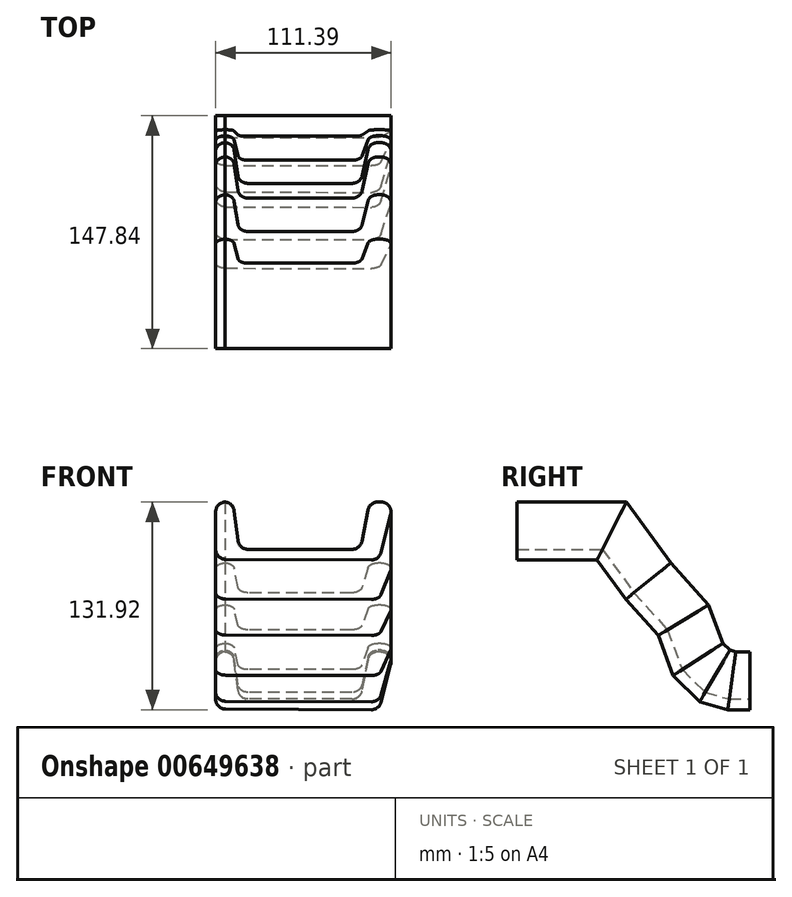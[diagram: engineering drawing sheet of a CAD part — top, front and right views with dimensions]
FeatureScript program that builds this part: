
annotation { "Feature Type Name" : "Feature", "Feature Type Description" : "" }
export const myFeature = defineFeature(function(context is Context, id is Id, definition is map)
    precondition{}
    {
        {
            var Q0;
            Q0=qCreatedBy(makeId("Front.planeOp"),FACE);
            var sketch = newSketch(context, id + "F0", { "sketchPlane" : qUnion([Q0])});
            skLineSegment(sketch, "E0", {"start": v(-51.67, 0) * mm, "end": v(-51.67, 23.72) * mm});
            skLineSegment(sketch, "E1", {"start": v(-46.16, 30.07) * mm, "end": v(-45.32, 30.07) * mm});
            skLineSegment(sketch, "E2", {"start": v(-39.86, 24.51) * mm, "end": v(-37.47, 5.56) * mm});
            skLineSegment(sketch, "E3", {"start": v(-31.17, 0) * mm, "end": v(34.97, 0) * mm});
            skLineSegment(sketch, "E4", {"start": v(41.2, 5.14) * mm, "end": v(45.05, 24.92) * mm});
            skLineSegment(sketch, "E5", {"start": v(51.29, 30.05) * mm, "end": v(53.37, 30.05) * mm});
            skLineSegment(sketch, "E6", {"start": v(59.53, 22.13) * mm, "end": v(53.36, -1.95) * mm});
            skLineSegment(sketch, "E7", {"start": v(47.18, -6.73) * mm, "end": v(-45.35, -6.35) * mm});
            skPoint(sketch, "E8.visualSharp", {"position": v(-51.67, 30.07) * mm});
            skArc(sketch, "E8.filletArc", {"start": v(-45.32, 30.07) * mm, "mid": v(-49.81, 28.2) * mm, "end": v(-51.67, 23.72) * mm});
            skPoint(sketch, "E9.visualSharp", {"position": v(61.56, 30.05) * mm});
            skArc(sketch, "E9.filletArc", {"start": v(59.53, 22.13) * mm, "mid": v(58.4, 27.6) * mm, "end": v(53.37, 30.05) * mm});
            skPoint(sketch, "E10.visualSharp", {"position": v(46.05, 30.05) * mm});
            skArc(sketch, "E10.filletArc", {"start": v(51.29, 30.05) * mm, "mid": v(47.25, 28.6) * mm, "end": v(45.05, 24.92) * mm});
            skPoint(sketch, "E11.visualSharp", {"position": v(52.13, -6.75) * mm});
            skArc(sketch, "E11.filletArc", {"start": v(47.18, -6.73) * mm, "mid": v(51.09, -5.4) * mm, "end": v(53.36, -1.95) * mm});
            skPoint(sketch, "E12.visualSharp", {"position": v(-40.57, 30.07) * mm});
            skArc(sketch, "E12.filletArc", {"start": v(-39.86, 24.51) * mm, "mid": v(-41.96, 28.48) * mm, "end": v(-46.16, 30.07) * mm});
            skPoint(sketch, "E13.visualSharp", {"position": v(-51.67, -6.32) * mm});
            skArc(sketch, "E13.filletArc", {"start": v(-51.67, 0) * mm, "mid": v(-49.82, -4.48) * mm, "end": v(-45.35, -6.35) * mm});
            skPoint(sketch, "E14.visualSharp", {"position": v(-36.77, 0) * mm});
            skArc(sketch, "E14.filletArc", {"start": v(-37.47, 5.56) * mm, "mid": v(-35.37, 1.59) * mm, "end": v(-31.17, 0) * mm});
            skPoint(sketch, "E15.visualSharp", {"position": v(40.2, 0) * mm});
            skArc(sketch, "E15.filletArc", {"start": v(34.97, 0) * mm, "mid": v(39, 1.45) * mm, "end": v(41.2, 5.14) * mm});
            skSolve(sketch);
        }
        {
            var Q0;
            Q0=qCreatedBy(makeId("Right.planeOp"),FACE);
            var sketch = newSketch(context, id + "F1", { "sketchPlane" : qUnion([Q0])});
            skLineSegment(sketch, "E16", {"start": v(0, 0) * mm, "end": v(54.23, 0) * mm});
            skLineSegment(sketch, "E17", {"start": v(54.23, 0) * mm, "end": v(74.33, -27.55) * mm});
            skLineSegment(sketch, "E18", {"start": v(74.33, -27.55) * mm, "end": v(95.55, -51.1) * mm});
            skLineSegment(sketch, "E19", {"start": v(95.55, -51.1) * mm, "end": v(104.92, -76.38) * mm});
            skLineSegment(sketch, "E20", {"start": v(104.92, -76.38) * mm, "end": v(119.56, -90.8) * mm});
            skLineSegment(sketch, "E21", {"start": v(119.56, -90.8) * mm, "end": v(134.8, -95.13) * mm});
            skLineSegment(sketch, "E22", {"start": v(134.8, -95.13) * mm, "end": v(147.84, -95.13) * mm});
            skSolve(sketch);
        }
        {
            var Q0;
            Q0=makeQuery(id+"F0.imprint","IMPRINT",FACE,{"disambiguationData":[TD([[makeQuery(id+"F0.imprint","IMPRINT",EDGE,{"derivedFrom":sQuery(id+"F0.wireOp",EDGE,"E0")}),-1.0]])]});
            var Q1;
            Q1=sQuery(id+"F1.wireOp",EDGE,"E18");
            var Q2;
            Q2=sQuery(id+"F1.wireOp",EDGE,"E17");
            var Q3;
            Q3=sQuery(id+"F1.wireOp",EDGE,"E16");
            var Q4;
            Q4=sQuery(id+"F1.wireOp",EDGE,"E19");
            var Q5;
            Q5=sQuery(id+"F1.wireOp",EDGE,"E20");
            var Q6;
            Q6=sQuery(id+"F1.wireOp",EDGE,"E22");
            var Q7;
            Q7=sQuery(id+"F1.wireOp",EDGE,"E21");
            sweep(context, id + "F2", {"profiles" : qUnion([Q0]), "path" : qUnion([Q1, Q2, Q3, Q4, Q5, Q6, Q7])});
        }
    });
